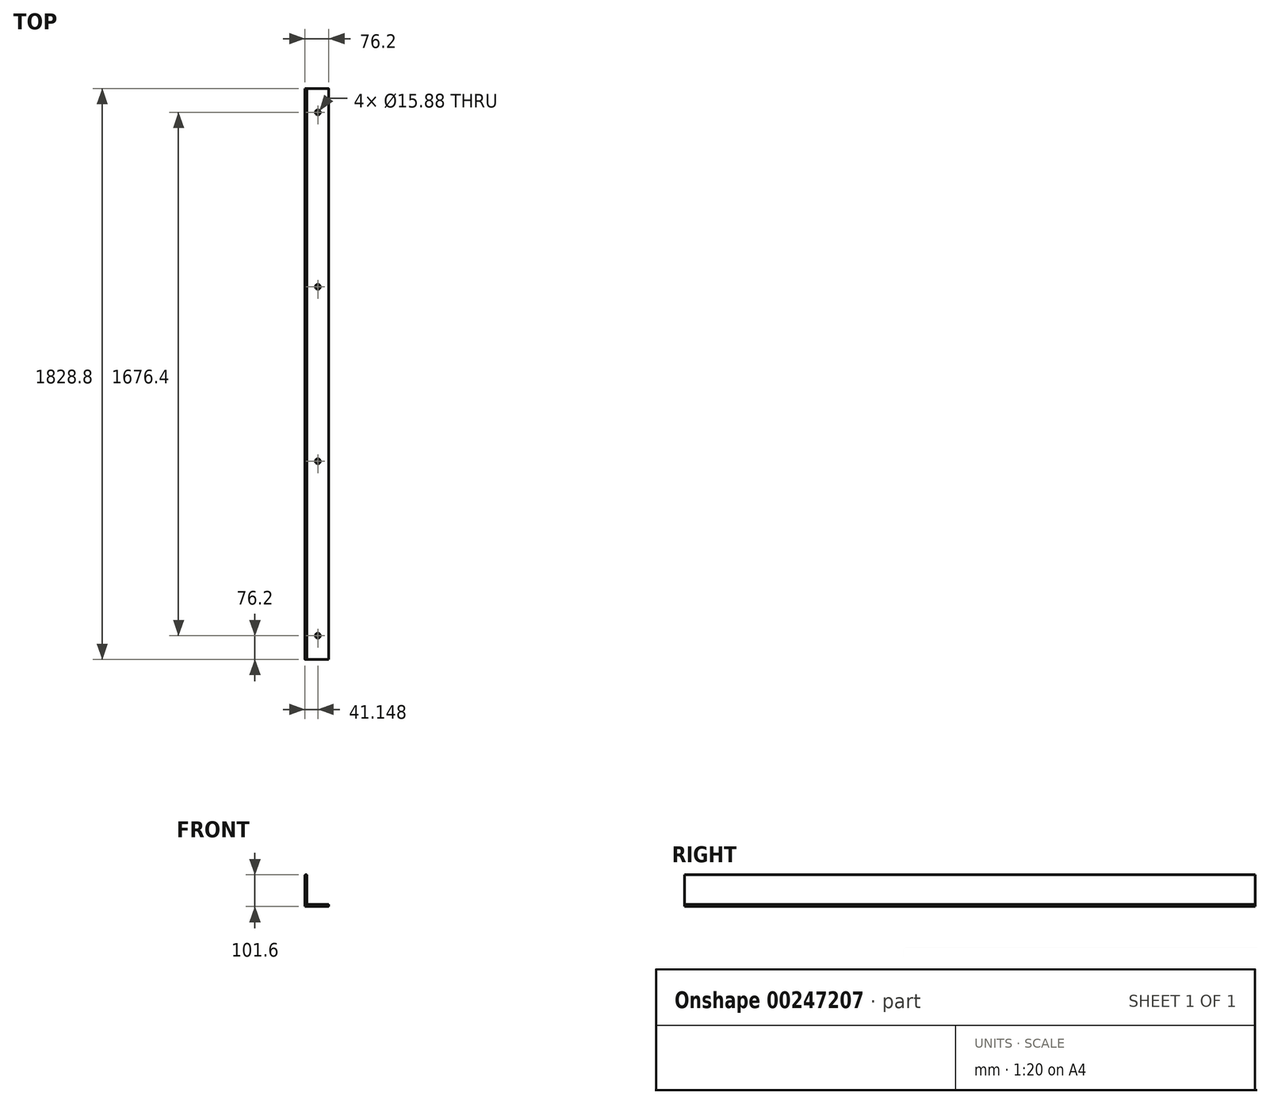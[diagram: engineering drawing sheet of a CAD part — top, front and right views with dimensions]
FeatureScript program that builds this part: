
annotation { "Feature Type Name" : "Feature", "Feature Type Description" : "" }
export const myFeature = defineFeature(function(context is Context, id is Id, definition is map)
    precondition{}
    {
        {
            var Q0;
            Q0=qCreatedBy(makeId("Front.planeOp"),FACE);
            var sketch = newSketch(context, id + "F0", { "sketchPlane" : qUnion([Q0])});
            skLineSegment(sketch, "E0", {"start": v(0, 0) * mm, "end": v(74.68, 0) * mm});
            skLineSegment(sketch, "E1", {"start": v(76.2, 1.52) * mm, "end": v(76.2, 4.83) * mm});
            skLineSegment(sketch, "E2", {"start": v(74.68, 6.35) * mm, "end": v(7.87, 6.35) * mm});
            skLineSegment(sketch, "E3", {"start": v(6.35, 7.87) * mm, "end": v(6.35, 100.08) * mm});
            skLineSegment(sketch, "E4", {"start": v(4.83, 101.6) * mm, "end": v(1.52, 101.6) * mm});
            skLineSegment(sketch, "E5", {"start": v(0, 100.08) * mm, "end": v(0, 0) * mm});
            skPoint(sketch, "E6.visualSharp", {"position": v(0, 101.6) * mm});
            skArc(sketch, "E6.filletArc", {"start": v(1.52, 101.6) * mm, "mid": v(0.45, 101.15) * mm, "end": v(0, 100.08) * mm});
            skPoint(sketch, "E7.visualSharp", {"position": v(6.35, 101.6) * mm});
            skArc(sketch, "E7.filletArc", {"start": v(6.35, 100.08) * mm, "mid": v(5.9, 101.15) * mm, "end": v(4.83, 101.6) * mm});
            skPoint(sketch, "E8.visualSharp", {"position": v(6.35, 6.35) * mm});
            skArc(sketch, "E8.filletArc", {"start": v(6.35, 7.87) * mm, "mid": v(6.8, 6.8) * mm, "end": v(7.87, 6.35) * mm});
            skPoint(sketch, "E9.visualSharp", {"position": v(76.2, 6.35) * mm});
            skArc(sketch, "E9.filletArc", {"start": v(76.2, 4.83) * mm, "mid": v(75.75, 5.9) * mm, "end": v(74.68, 6.35) * mm});
            skPoint(sketch, "E10.visualSharp", {"position": v(76.2, 0) * mm});
            skArc(sketch, "E10.filletArc", {"start": v(74.68, 0) * mm, "mid": v(75.75, 0.45) * mm, "end": v(76.2, 1.52) * mm});
            skSolve(sketch);
        }
        {
            var Q0;
            Q0=makeQuery(id+"F0.imprint","IMPRINT",FACE,{"disambiguationData":[TD([[makeQuery(id+"F0.imprint","IMPRINT",EDGE,{"derivedFrom":sQuery(id+"F0.wireOp",EDGE,"E0")}),1.0]])]});
            extrude(context, id + "F1", {"entities" : qUnion([Q0]), "depth" : 1828.8 * mm});
        }
        {
            var Q0;
            Q0=makeQuery(id+"F1.opExtrude","SWEPT_FACE",FACE,{"disambiguationData":[OSD([sQuery(id+"F0.wireOp",EDGE,"E2")])]});
            var sketch = newSketch(context, id + "F2", { "sketchPlane" : qUnion([Q0])});
            skPoint(sketch, "E11", {"position": v(41.15, -76.2) * mm});
            skPoint(sketch, "E12", {"position": v(41.15, -1752.6) * mm});
            skPoint(sketch, "E13", {"position": v(41.15, -1193.8) * mm});
            skPoint(sketch, "E14", {"position": v(41.15, -635) * mm});
            skSolve(sketch);
        }
        {
            var Q0;
            Q0=sQuery(id+"F2.wireOp",VERTEX,"E12");
            var Q1;
            Q1=sQuery(id+"F2.wireOp",VERTEX,"E13");
            var Q2;
            Q2=sQuery(id+"F2.wireOp",VERTEX,"E14");
            var Q3;
            Q3=sQuery(id+"F2.wireOp",VERTEX,"E11");
            var Q4;
            Q4=makeQuery(id+"F1.opExtrude","SWEPT_BODY",BODY,{"disambiguationData":[OSD([sQuery(id+"F0.wireOp",EDGE,"E0"),sQuery(id+"F0.wireOp",EDGE,"E1"),sQuery(id+"F0.wireOp",EDGE,"E2"),sQuery(id+"F0.wireOp",EDGE,"E3"),sQuery(id+"F0.wireOp",EDGE,"E4"),sQuery(id+"F0.wireOp",EDGE,"E5"),sQuery(id+"F0.wireOp",EDGE,"E6.filletArc"),sQuery(id+"F0.wireOp",EDGE,"E7.filletArc"),sQuery(id+"F0.wireOp",EDGE,"E8.filletArc"),sQuery(id+"F0.wireOp",EDGE,"E9.filletArc"),sQuery(id+"F0.wireOp",EDGE,"E10.filletArc")])]});
            hole(context, id + "F3", {"style" : HoleStyle.SIMPLE, "endStyle" : HoleEndStyle.THROUGH, "holeDiameter" : 15.88 * mm, "tappedDepth" : 12.7 * mm, "tapClearance" : 3, "locations" : qUnion([Q0, Q1, Q2, Q3]), "scope" : qUnion([Q4])});
        }
    });
